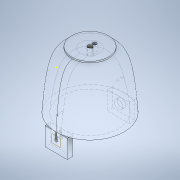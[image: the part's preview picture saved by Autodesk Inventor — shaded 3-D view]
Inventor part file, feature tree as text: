
AUTODESK INVENTOR PART (.ipt)
format: ipt  version: 2021.1 (Build 251245010, 245A)  size: 525,824 bytes
history: native  units: mm
features: sketch x13, extrude x9, plane x5, mirror x5, revolve x1, hole x1, thread x1
ambient origin geometry x8: Origin, YZ Plane, XZ Plane, XY Plane, X Axis, Y Axis, Z Axis, Center Point
bodies: Solid1 (feature_tree)
feature tree (35):
  extrude  "Extrusion1"  Depth=25.0mm
  plane  "Work Plane2"
  revolve  "Revolution1"  [1 undecoded]
  mirror  "Mirror1"
  plane  "Work Plane3"
  hole  "Hole1"  [1 undecoded]
  thread  "Thread1"  [1 undecoded]
  extrude  "Extrusion2"  Depth=10.0mm
  mirror  "Mirror2"
  extrude  "Extrusion4"  Depth=25.0mm
  sketch  "Sketch9"  dims[d36=0.0mm d40=10.0mm]
  plane  "Work Plane4"
  extrude  "Extrusion5"  Depth=55.0mm
  mirror  "Mirror4"
  extrude  "Extrusion6"  Depth=12.0mm
  sketch  "Sketch12"  dims[d46=5.0mm d49=12.0mm]
  mirror  "Mirror5"
  sketch  "Sketch13"  dims[d50=0.0mm d51=14.5mm]
  plane  "Work Plane5"
  extrude  "Extrusion7"  Depth=14.5mm
  mirror  "Mirror6"
  extrude  "Extrusion8"  Depth=1.5mm
  extrude  "Extrusion9"  Depth=14.5mm
  extrude  "Extrusion10"  TaperAngle=90.0deg  [1 undecoded]
  plane  "Work Plane1"
  sketch  "Sketch3"  dims[d3=0.0mm d4=25.0mm d5=-50.0mm]
  sketch  "Sketch4"  dims[d9=15.0mm d10=15.0mm]
  sketch  "Sketch6"  dims[d11=360.0deg d12=92.0455mm]
  sketch  "Sketch8"  dims[d16=3.0mm d17=6.0mm d18=4.0mm d19=2.0mm d20=90.0deg d21=8.0mm d22=20.594885mm d23=178.334mm d24=0.0mm]
  sketch  "Sketch10"  dims[d41=0.0mm d42=0.0mm d43=25.0mm]
  sketch  "Sketch11"  dims[d44=5.0mm d45=55.0mm]
  sketch  "Sketch14"  dims[d56=6.8mm d57=1.5mm]
  sketch  "Sketch15"  dims[d58=12.0mm d59=0.0mm d60=14.5mm]
  sketch  "Sketch16"  dims[d61=10.0mm d62=0.0mm d63=90.0deg]
  sketch  "Sketch17"  dims[d65=1.0mm d66=0.0mm d68=0.0mm d69=0.0mm d71=6.0mm d72=2.5mm d74=17.0mm d75=0.0mm d78=0.0mm]
note: 4 required parameter values undecoded (feature->parameter linkage not recoverable at this tier; creation-order binding heuristic only, values carry confidence <= 0.55)